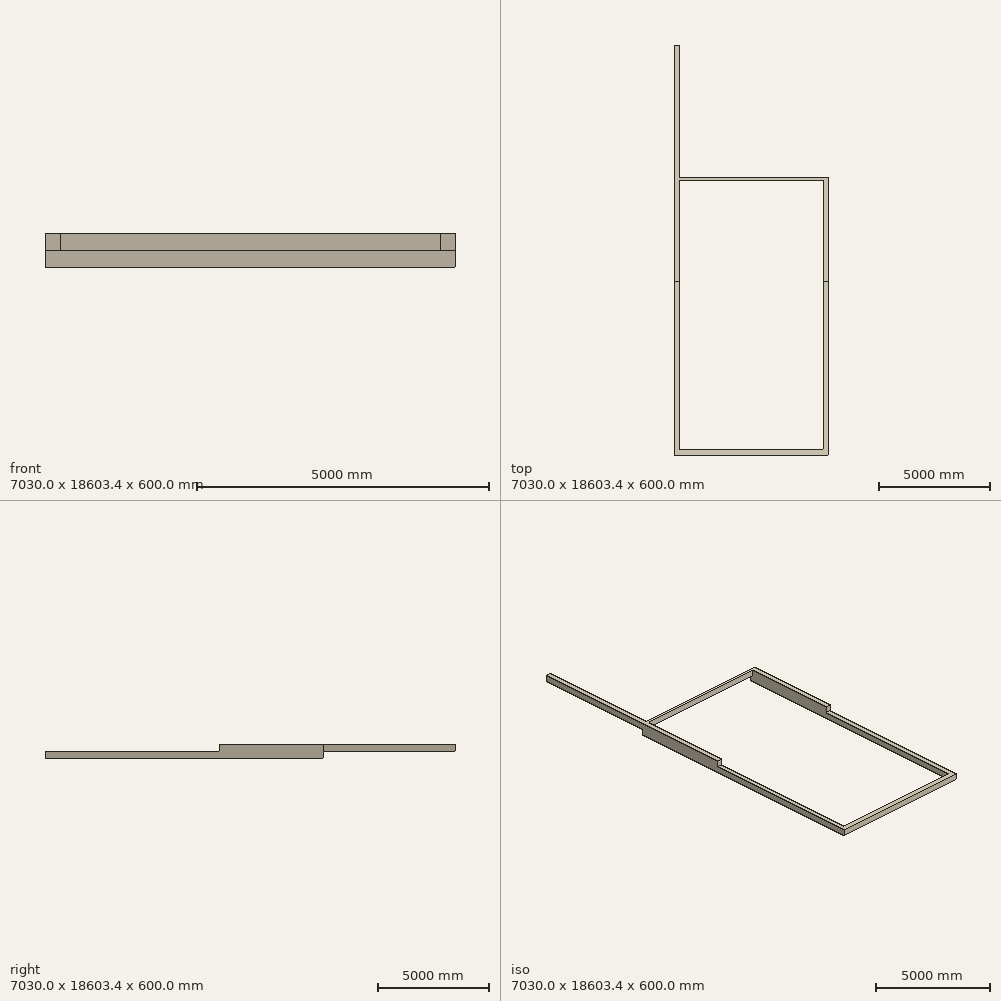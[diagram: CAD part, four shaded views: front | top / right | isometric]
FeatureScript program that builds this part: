
annotation { "Feature Type Name" : "Feature", "Feature Type Description" : "" }
export const myFeature = defineFeature(function(context is Context, id is Id, definition is map)
    precondition{}
    {
        {
            var Q0;
            Q0=qCreatedBy(makeId("Top.planeOp"),FACE);
            var sketch = newSketch(context, id + "F0", { "sketchPlane" : qUnion([Q0])});
            skLineSegment(sketch, "E0.bottom", {"start": v(3265, -2930) * mm, "end": v(-3265, -2930) * mm});
            skLineSegment(sketch, "E0.left", {"start": v(3265, -2930) * mm, "end": v(3265, 9428.4) * mm});
            skLineSegment(sketch, "E0.right", {"start": v(-3265, -2930) * mm, "end": v(-3265, 2930) * mm});
            skPoint(sketch, "E0.middle", {"position": v(0, 0) * mm});
            skLineSegment(sketch, "E1", {"start": v(-3265, 2930) * mm, "end": v(-3265, 13518.4) * mm});
            skLineSegment(sketch, "E2", {"start": v(-3515, 9428.4) * mm, "end": v(3515, 9428.4) * mm});
            skLineSegment(sketch, "E3", {"start": v(3265, 4708.4) * mm, "end": v(3515, 4708.4) * mm});
            skLineSegment(sketch, "E4.0", {"start": v(-3515, -3180) * mm, "end": v(-3515, 9428.4) * mm});
            skLineSegment(sketch, "E5.0", {"start": v(3515, -3180) * mm, "end": v(-3515, -3180) * mm});
            skLineSegment(sketch, "E6.0", {"start": v(-3265, 9178.4) * mm, "end": v(3515, 9178.4) * mm});
            skLineSegment(sketch, "E7.0", {"start": v(3515, -3180) * mm, "end": v(3515, 9428.4) * mm});
            skLineSegment(sketch, "E8", {"start": v(-3265, 13518.4) * mm, "end": v(-3515, 13518.4) * mm});
            skLineSegment(sketch, "E9", {"start": v(-3515, 13518.4) * mm, "end": v(-3515, 9428.4) * mm});
            skLineSegment(sketch, "E10", {"start": v(-3265, 13518.4) * mm, "end": v(-3265, 15673.4) * mm});
            skLineSegment(sketch, "E11", {"start": v(-3265, 15673.4) * mm, "end": v(-3515, 15673.4) * mm});
            skLineSegment(sketch, "E12", {"start": v(-3515, 15673.4) * mm, "end": v(-3515, 13518.4) * mm});
            skCircle(sketch, "E13", {"center": v(-1492.5, 5872.47) * mm, "radius": 460.87 * mm});
            skCircle(sketch, "E14", {"center": v(1289.32, 5892.61) * mm, "radius": 460.87 * mm});
            skLineSegment(sketch, "E15", {"start": v(3265, 4708.4) * mm, "end": v(-3265, 4708.4) * mm, "construction": true});
            skLineSegment(sketch, "E16", {"start": v(-3265, 9303.4) * mm, "end": v(3515, 9303.4) * mm});
            skLineSegment(sketch, "E17", {"start": v(-3265, 4708.4) * mm, "end": v(-3515, 4708.4) * mm});
            skLineSegment(sketch, "E18.bottom", {"start": v(-3515, 15673.4) * mm, "end": v(-2515.19, 15673.4) * mm});
            skLineSegment(sketch, "E18.top", {"start": v(-3515, 15423.4) * mm, "end": v(-2515.19, 15423.4) * mm});
            skLineSegment(sketch, "E18.left", {"start": v(-3515, 15673.4) * mm, "end": v(-3515, 15423.4) * mm});
            skLineSegment(sketch, "E18.right", {"start": v(-2515.19, 15673.4) * mm, "end": v(-2515.19, 15423.4) * mm});
            skSolve(sketch);
        }
        {
            var Q0;
            {var subQ2=sQuery(id+"F0.wireOp",EDGE,"E0.bottom");Q0=makeQuery(id+"F0.imprint","IMPRINT",FACE,{"disambiguationData":[TD([[makeQuery(id+"F0.imprint","IMPRINT",EDGE,{"derivedFrom":subQ2}),1.0]])]});}
            var Q1;
            {var subQ5=sQuery(id+"F0.wireOp",EDGE,"E17");Q1=makeQuery(id+"F0.imprint","IMPRINT",FACE,{"disambiguationData":[TD([[makeQuery(id+"F0.imprint","IMPRINT",EDGE,{"derivedFrom":subQ5}),-1.0]])]});}
            var Q2;
            {var subQ0=sQuery(id+"F0.wireOp",EDGE,"E3");Q2=makeQuery(id+"F0.imprint","IMPRINT",FACE,{"disambiguationData":[TD([[makeQuery(id+"F0.imprint","IMPRINT",EDGE,{"derivedFrom":subQ0}),1.0]])]});}
            var Q3;
            {var subQ0=sQuery(id+"F0.wireOp",EDGE,"E6.0");var subQ1=sQuery(id+"F0.wireOp",EDGE,"E0.left");var subQ2=makeQuery(id+"F0.imprint","INTERSECT",VERTEX,{"derivedFrom":[subQ1,subQ0]});Q3=makeQuery(id+"F0.imprint","IMPRINT",FACE,{"disambiguationData":[TD([[makeQuery(id+"F0.imprint","IMPRINT",EDGE,{"disambiguationData":[TD([[subQ2,-1.0]])],"derivedFrom":subQ1}),-1.0]])]});}
            var Q4;
            {var subQ0=sQuery(id+"F0.wireOp",EDGE,"E2");var subQ1=sQuery(id+"F0.wireOp",EDGE,"E0.left");var subQ2=makeQuery(id+"F0.imprint","INTERSECT",VERTEX,{"derivedFrom":[subQ1,subQ0]});Q4=makeQuery(id+"F0.imprint","IMPRINT",FACE,{"disambiguationData":[TD([[makeQuery(id+"F0.imprint","IMPRINT",EDGE,{"disambiguationData":[TD([[subQ2,1.0]])],"derivedFrom":subQ1}),-1.0]])]});}
            extrude(context, id + "F1", {"entities" : qUnion([Q0, Q1, Q2, Q3, Q4]), "oppositeDirection" : true, "depth" : 300 * mm, "offsetDistance" : 25 * mm});
        }
        {
            var Q0;
            Q0=makeQuery(id+"F0.imprint","IMPRINT",FACE,{"disambiguationData":[TD([[makeQuery(id+"F0.imprint","IMPRINT",EDGE,{"derivedFrom":sQuery(id+"F0.wireOp",EDGE,"E8")}),-1.0]])]});
            var Q1;
            {var subQ0=sQuery(id+"F0.wireOp",EDGE,"E8");Q1=makeQuery(id+"F0.imprint","IMPRINT",FACE,{"disambiguationData":[TD([[makeQuery(id+"F0.imprint","IMPRINT",EDGE,{"derivedFrom":subQ0}),1.0]])]});}
            var Q2;
            {var subQ5=sQuery(id+"F0.wireOp",EDGE,"E17");Q2=makeQuery(id+"F0.imprint","IMPRINT",FACE,{"disambiguationData":[TD([[makeQuery(id+"F0.imprint","IMPRINT",EDGE,{"derivedFrom":subQ5}),-1.0]])]});}
            var Q3;
            {var subQ0=sQuery(id+"F0.wireOp",EDGE,"E3");Q3=makeQuery(id+"F0.imprint","IMPRINT",FACE,{"disambiguationData":[TD([[makeQuery(id+"F0.imprint","IMPRINT",EDGE,{"derivedFrom":subQ0}),1.0]])]});}
            var Q4;
            {var subQ0=sQuery(id+"F0.wireOp",EDGE,"E6.0");var subQ1=sQuery(id+"F0.wireOp",EDGE,"E0.left");var subQ2=makeQuery(id+"F0.imprint","INTERSECT",VERTEX,{"derivedFrom":[subQ1,subQ0]});Q4=makeQuery(id+"F0.imprint","IMPRINT",FACE,{"disambiguationData":[TD([[makeQuery(id+"F0.imprint","IMPRINT",EDGE,{"disambiguationData":[TD([[subQ2,-1.0]])],"derivedFrom":subQ1}),-1.0]])]});}
            var Q5;
            {var subQ0=sQuery(id+"F0.wireOp",EDGE,"E2");var subQ1=sQuery(id+"F0.wireOp",EDGE,"E0.left");var subQ2=makeQuery(id+"F0.imprint","INTERSECT",VERTEX,{"derivedFrom":[subQ1,subQ0]});Q5=makeQuery(id+"F0.imprint","IMPRINT",FACE,{"disambiguationData":[TD([[makeQuery(id+"F0.imprint","IMPRINT",EDGE,{"disambiguationData":[TD([[subQ2,1.0]])],"derivedFrom":subQ1}),-1.0]])]});}
            var Q6;
            {var subQ0=sQuery(id+"F0.wireOp",EDGE,"E2");var subQ1=sQuery(id+"F0.wireOp",EDGE,"E0.left");var subQ2=makeQuery(id+"F0.imprint","INTERSECT",VERTEX,{"derivedFrom":[subQ1,subQ0]});Q6=makeQuery(id+"F0.imprint","IMPRINT",FACE,{"disambiguationData":[TD([[makeQuery(id+"F0.imprint","IMPRINT",EDGE,{"disambiguationData":[TD([[subQ2,1.0]])],"derivedFrom":subQ1}),1.0]])]});}
            extrude(context, id + "F2", {"entities" : qUnion([Q0, Q1, Q2, Q3, Q4, Q5, Q6]), "operationType" : NewBodyOperationType.ADD, "depth" : 300 * mm, "offsetDistance" : 25 * mm});
        }
    });
